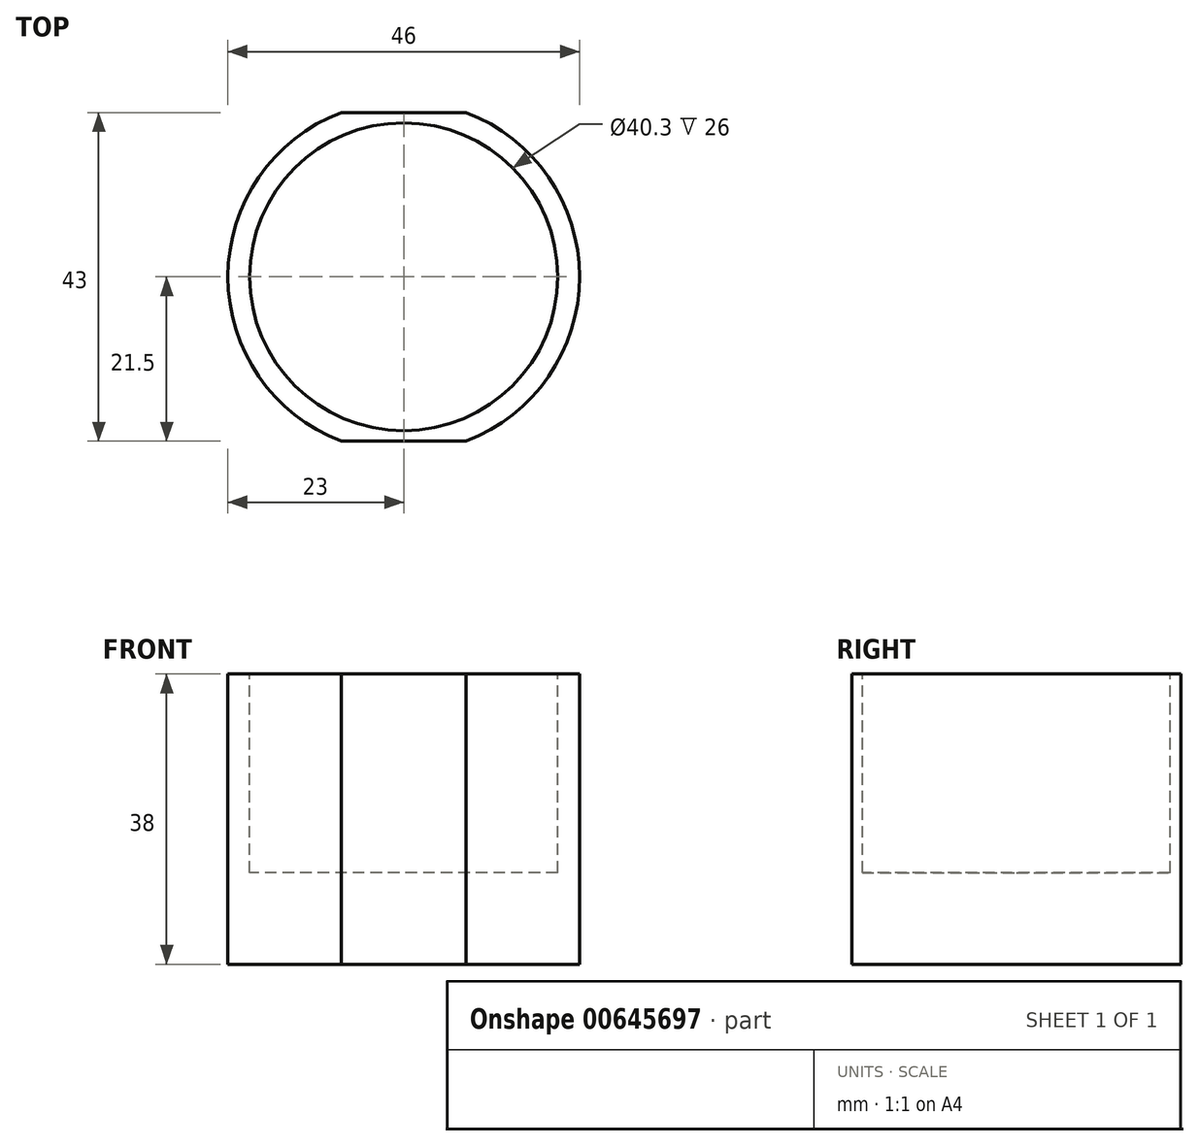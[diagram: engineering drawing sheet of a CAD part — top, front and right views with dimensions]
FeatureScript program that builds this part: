
annotation { "Feature Type Name" : "Feature", "Feature Type Description" : "" }
export const myFeature = defineFeature(function(context is Context, id is Id, definition is map)
    precondition{}
    {
        {
            var Q0;
            Q0=qCreatedBy(makeId("Top.planeOp"),FACE);
            var sketch = newSketch(context, id + "F0", { "sketchPlane" : qUnion([Q0])});
            skArc(sketch, "E0", {"start": v(-8.17, 21.5) * mm, "mid": v(-23, 0) * mm, "end": v(-8.17, -21.5) * mm});
            skLineSegment(sketch, "E1", {"start": v(-8.17, 21.5) * mm, "end": v(8.17, 21.5) * mm});
            skLineSegment(sketch, "E2.MirrorCS", {"start": v(-8.17, -21.5) * mm, "end": v(8.17, -21.5) * mm});
            skArc(sketch, "E3.trimOffspring", {"start": v(8.17, -21.5) * mm, "mid": v(23, 0) * mm, "end": v(8.17, 21.5) * mm});
            skSolve(sketch);
        }
        {
            var Q0;
            Q0=qSketchRegion(id+"F0",true);
            extrude(context, id + "F1", {"entities" : qUnion([Q0]), "depth" : 38 * mm, "offsetDistance" : 25 * mm});
        }
        {
            var Q0;
            Q0=makeQuery(id+"F1.opExtrude","CAP_FACE",FACE,{"disambiguationData":[OSD([sQuery(id+"F0.wireOp",EDGE,"E0"),sQuery(id+"F0.wireOp",EDGE,"E1"),sQuery(id+"F0.wireOp",EDGE,"E2.MirrorCS"),sQuery(id+"F0.wireOp",EDGE,"E3.trimOffspring")])],"isStart":false});
            var sketch = newSketch(context, id + "F2", { "sketchPlane" : qUnion([Q0])});
            skCircle(sketch, "E4", {"center": v(0, 0) * mm, "radius": 20.15 * mm});
            skSolve(sketch);
        }
        {
            var Q0;
            Q0=makeQuery(id+"F2.imprint","IMPRINT",FACE,{"disambiguationData":[TD([[makeQuery(id+"F2.imprint","IMPRINT",EDGE,{"derivedFrom":sQuery(id+"F2.wireOp",EDGE,"E4")}),1.0]])]});
            extrude(context, id + "F3", {"entities" : qUnion([Q0]), "operationType" : NewBodyOperationType.REMOVE, "oppositeDirection" : true, "depth" : 26 * mm, "offsetDistance" : 25 * mm});
        }
        {
            var Q0;
            Q0=makeQuery(id+"F1.opExtrude","CAP_FACE",FACE,{"disambiguationData":[OSD([sQuery(id+"F0.wireOp",EDGE,"E0"),sQuery(id+"F0.wireOp",EDGE,"E1"),sQuery(id+"F0.wireOp",EDGE,"E2.MirrorCS"),sQuery(id+"F0.wireOp",EDGE,"E3.trimOffspring")])],"isStart":true});
            var sketch = newSketch(context, id + "F4", { "sketchPlane" : qUnion([Q0])});
            skArc(sketch, "E5", {"start": v(11.5, 15.75) * mm, "mid": v(0, 19.5) * mm, "end": v(-11.5, 15.75) * mm});
            skLineSegment(sketch, "E6", {"start": v(-11.5, 15.75) * mm, "end": v(-11.5, -15.75) * mm});
            skLineSegment(sketch, "E7.MirrorCS", {"start": v(11.5, 15.75) * mm, "end": v(11.5, -15.75) * mm});
            skArc(sketch, "E8.trimOffspring", {"start": v(-11.5, -15.75) * mm, "mid": v(0, -19.5) * mm, "end": v(11.5, -15.75) * mm});
            skSolve(sketch);
        }
    });
